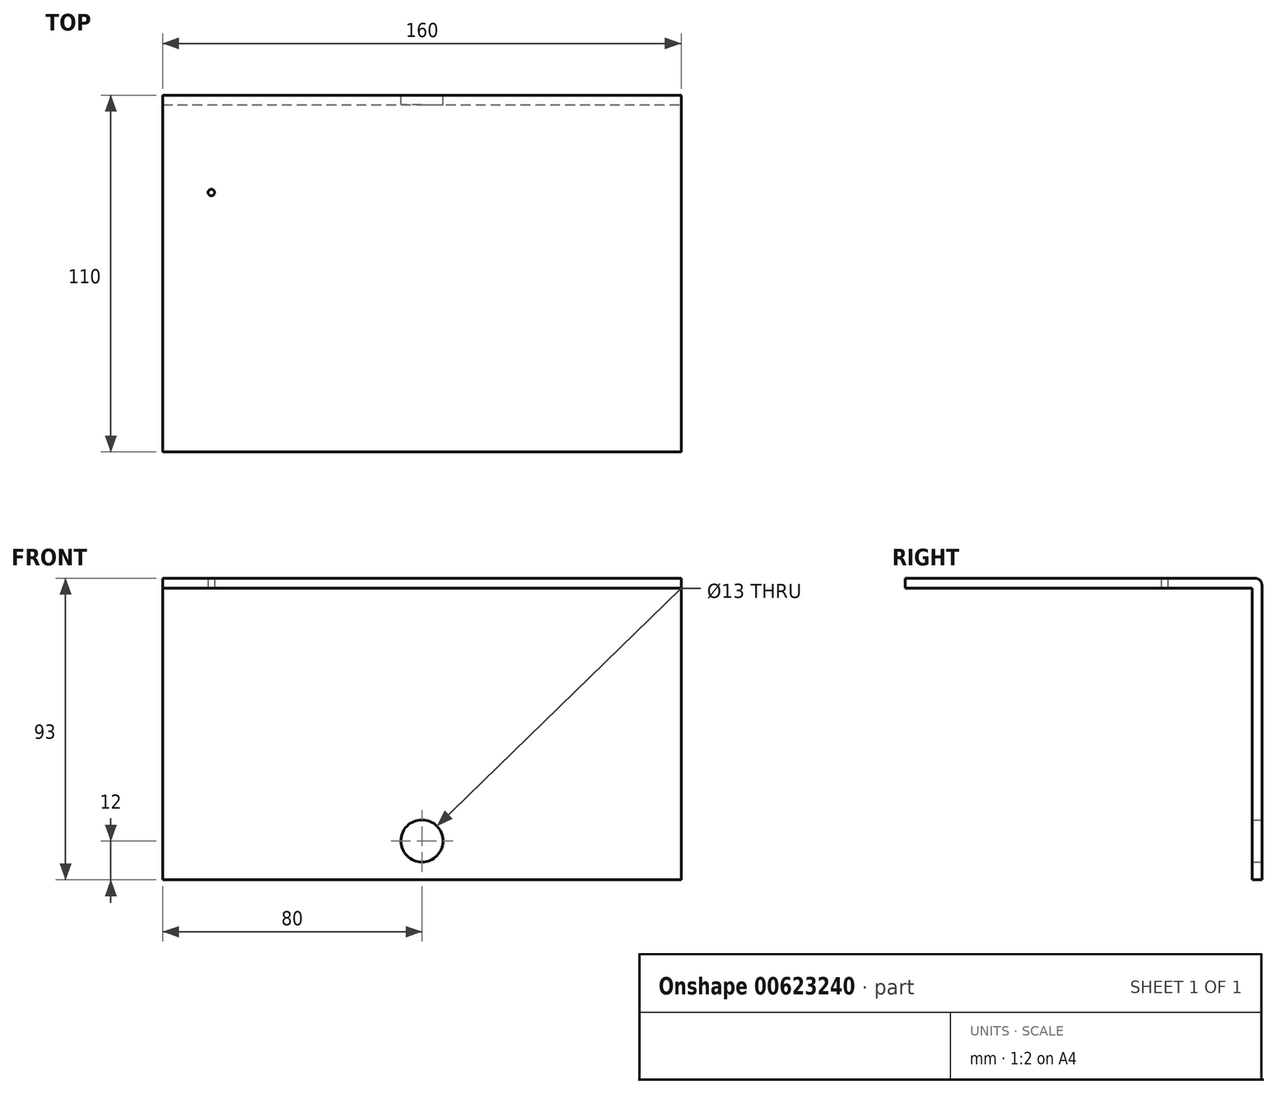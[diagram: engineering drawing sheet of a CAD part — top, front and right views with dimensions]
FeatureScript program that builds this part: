
annotation { "Feature Type Name" : "Feature", "Feature Type Description" : "" }
export const myFeature = defineFeature(function(context is Context, id is Id, definition is map)
    precondition{}
    {
        {
            var Q0;
            Q0=qCreatedBy(makeId("Top.planeOp"),FACE);
            var sketch = newSketch(context, id + "F0", { "sketchPlane" : qUnion([Q0])});
            skLineSegment(sketch, "E0.bottom", {"start": v(-80, 55) * mm, "end": v(80, 55) * mm});
            skLineSegment(sketch, "E0.top", {"start": v(-80, -55) * mm, "end": v(80, -55) * mm});
            skLineSegment(sketch, "E0.left", {"start": v(-80, 55) * mm, "end": v(-80, -55) * mm});
            skLineSegment(sketch, "E0.right", {"start": v(80, 55) * mm, "end": v(80, -55) * mm});
            skPoint(sketch, "E0.middle", {"position": v(0, 0) * mm});
            skCircle(sketch, "E1", {"center": v(-65, 25) * mm, "radius": 1 * mm});
            skSolve(sketch);
        }
        {
            var Q0;
            Q0=makeQuery(id+"F0.imprint","IMPRINT",FACE,{"disambiguationData":[TD([[makeQuery(id+"F0.imprint","IMPRINT",EDGE,{"derivedFrom":sQuery(id+"F0.wireOp",EDGE,"E0.bottom")}),-1.0]])]});
            extrude(context, id + "F1", {"entities" : qUnion([Q0]), "depth" : 3 * mm, "offsetDistance" : 25 * mm});
        }
        {
            var Q0;
            Q0=makeQuery(id+"F1.opExtrude","CAP_FACE",FACE,{"disambiguationData":[OSD([sQuery(id+"F0.wireOp",EDGE,"E0.bottom"),sQuery(id+"F0.wireOp",EDGE,"E0.top"),sQuery(id+"F0.wireOp",EDGE,"E0.left"),sQuery(id+"F0.wireOp",EDGE,"E0.right"),sQuery(id+"F0.wireOp",EDGE,"E1")])],"isStart":true});
            var sketch = newSketch(context, id + "F2", { "sketchPlane" : qUnion([Q0])});
            skLineSegment(sketch, "E2.bottom", {"start": v(-80, -55) * mm, "end": v(80, -55) * mm});
            skLineSegment(sketch, "E2.top", {"start": v(-80, -52) * mm, "end": v(80, -52) * mm});
            skLineSegment(sketch, "E2.left", {"start": v(-80, -55) * mm, "end": v(-80, -52) * mm});
            skLineSegment(sketch, "E2.right", {"start": v(80, -55) * mm, "end": v(80, -52) * mm});
            skSolve(sketch);
        }
        {
            var Q0;
            Q0 = qSketchRegion(id + "F2", true);
            extrude(context, id + "F3", {"entities" : qUnion([Q0]), "operationType" : NewBodyOperationType.ADD, "depth" : 90 * mm, "offsetDistance" : 25 * mm});
        }
        {
            var Q0;
            Q0=makeQuery(id+"F3.boolean.opBoolean","MERGE",FACE,{"derivedFrom":[makeQuery(id+"F1.opExtrude","SWEPT_FACE",FACE,{"disambiguationData":[OSD([sQuery(id+"F0.wireOp",EDGE,"E0.bottom")])]}),makeQuery(id+"F3.opExtrude","SWEPT_FACE",FACE,{"disambiguationData":[OSD([sQuery(id+"F2.wireOp",EDGE,"E2.bottom")])]})]});
            var sketch = newSketch(context, id + "F4", { "sketchPlane" : qUnion([Q0])});
            skCircle(sketch, "E3", {"center": v(0, -78) * mm, "radius": 6.5 * mm});
            skSolve(sketch);
        }
        {
            var Q0;
            Q0=makeQuery(id+"F4.imprint","IMPRINT",FACE,{"disambiguationData":[TD([[makeQuery(id+"F4.imprint","IMPRINT",EDGE,{"derivedFrom":sQuery(id+"F4.wireOp",EDGE,"E3")}),1.0]])]});
            extrude(context, id + "F5", {"entities" : qUnion([Q0]), "operationType" : NewBodyOperationType.REMOVE, "endBound" : BoundingType.THROUGH_ALL, "oppositeDirection" : true, "depth" : 25 * mm, "offsetDistance" : 25 * mm});
        }
        {
            var Q0;
            Q0=makeQuery(id+"F1.opExtrude","CAP_EDGE",EDGE,{"disambiguationData":[OSD([sQuery(id+"F0.wireOp",EDGE,"E0.bottom")])],"isStart":false});
            var Q1;
            Q1=makeQuery(id+"F3.opExtrude","CAP_EDGE",EDGE,{"disambiguationData":[OSD([sQuery(id+"F2.wireOp",EDGE,"E2.top")])],"isStart":true});
            fillet(context, id + "F6", {"entities" : qUnion([Q0, Q1]), "radius" : 2 * mm, "tangentPropagation" : true, "allowEdgeOverflow" : false});
        }
    });
